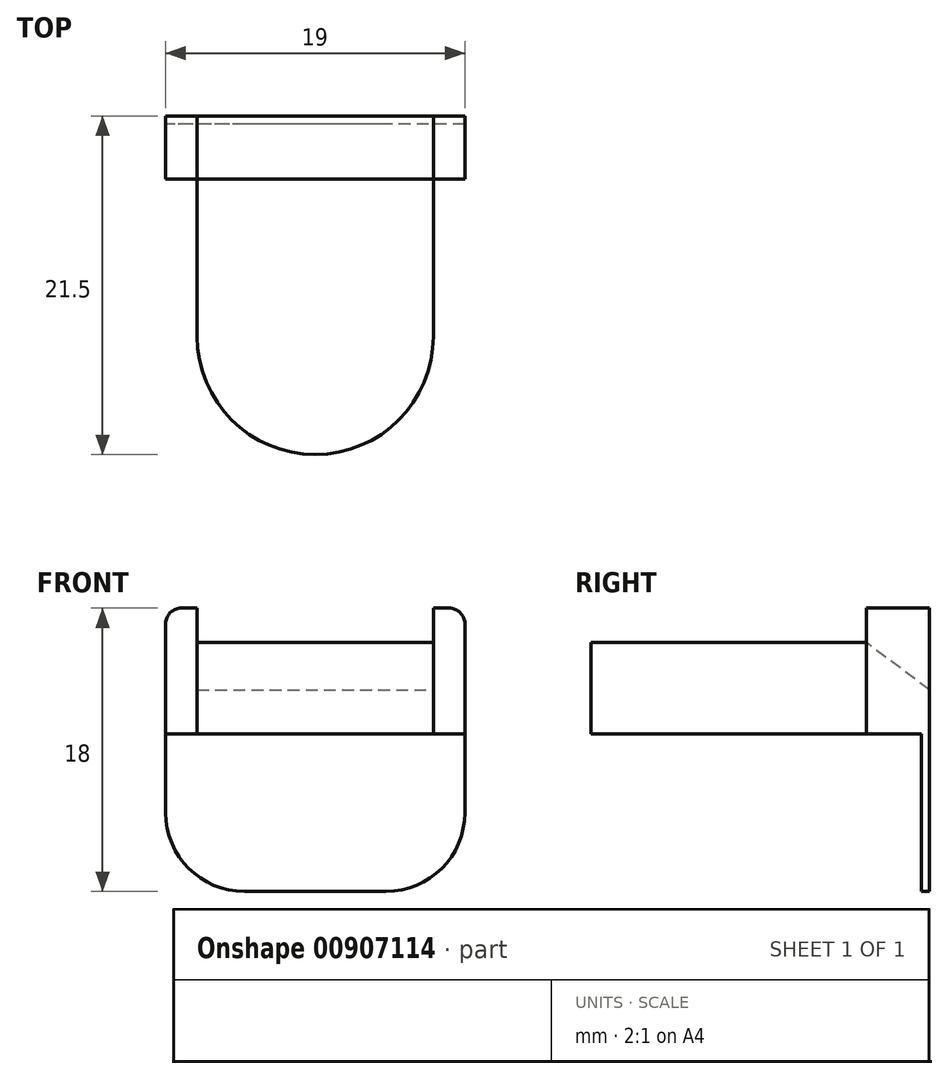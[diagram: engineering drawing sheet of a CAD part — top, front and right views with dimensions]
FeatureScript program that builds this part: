
annotation { "Feature Type Name" : "Feature", "Feature Type Description" : "" }
export const myFeature = defineFeature(function(context is Context, id is Id, definition is map)
    precondition{}
    {
        {
            var Q0;
            Q0=qCreatedBy(makeId("Top.planeOp"),FACE);
            var sketch = newSketch(context, id + "F0", { "sketchPlane" : qUnion([Q0])});
            skLineSegment(sketch, "E0", {"start": v(-7.5, 0) * mm, "end": v(-7.5, 14) * mm});
            skLineSegment(sketch, "E1", {"start": v(-7.5, 14) * mm, "end": v(7.5, 14) * mm});
            skLineSegment(sketch, "E2", {"start": v(7.5, 14) * mm, "end": v(7.5, 0) * mm});
            skArc(sketch, "E3", {"start": v(-7.5, 0) * mm, "mid": v(0, -7.5) * mm, "end": v(7.5, 0) * mm});
            skLineSegment(sketch, "E4", {"start": v(-7.5, 10) * mm, "end": v(-9.5, 10) * mm});
            skLineSegment(sketch, "E5", {"start": v(-9.5, 10) * mm, "end": v(-9.5, 14) * mm});
            skLineSegment(sketch, "E6", {"start": v(-9.5, 14) * mm, "end": v(-7.5, 14) * mm});
            skLineSegment(sketch, "E7", {"start": v(7.5, 14) * mm, "end": v(9.5, 14) * mm});
            skLineSegment(sketch, "E8", {"start": v(9.5, 14) * mm, "end": v(9.5, 10) * mm});
            skLineSegment(sketch, "E9", {"start": v(9.5, 10) * mm, "end": v(7.5, 10) * mm});
            skLineSegment(sketch, "E10", {"start": v(9.5, 13.5) * mm, "end": v(-9.5, 13.5) * mm});
            skSolve(sketch);
        }
        {
            var Q0;
            {var subQ0=sQuery(id+"F0.wireOp",EDGE,"E3");Q0=makeQuery(id+"F0.imprint","IMPRINT",FACE,{"disambiguationData":[TD([[makeQuery(id+"F0.imprint","IMPRINT",EDGE,{"derivedFrom":subQ0}),1.0]])]});}
            var Q1;
            {var subQ0=sQuery(id+"F0.wireOp",EDGE,"E1");Q1=makeQuery(id+"F0.imprint","IMPRINT",FACE,{"disambiguationData":[TD([[makeQuery(id+"F0.imprint","IMPRINT",EDGE,{"derivedFrom":subQ0}),-1.0]])]});}
            extrude(context, id + "F1", {"entities" : qUnion([Q0, Q1]), "depth" : 5.8 * mm, "offsetDistance" : 25 * mm});
        }
        {
            var Q0;
            Q0=makeQuery(id+"F1.opExtrude","CAP_EDGE",EDGE,{"disambiguationData":[OSD([sQuery(id+"F0.wireOp",EDGE,"E1")])],"isStart":false});
            chamfer(context, id + "F2", {"entities" : qUnion([Q0]), "chamferType" : ChamferType.TWO_OFFSETS, "width1" : 3 * mm, "oppositeDirection" : false, "width2" : 4 * mm, "tangentPropagation" : true});
        }
        {
            var Q0;
            {var subQ2=sQuery(id+"F0.wireOp",EDGE,"E4");Q0=makeQuery(id+"F0.imprint","IMPRINT",FACE,{"disambiguationData":[TD([[makeQuery(id+"F0.imprint","IMPRINT",EDGE,{"derivedFrom":subQ2}),-1.0]])]});}
            var Q1;
            {var subQ0=sQuery(id+"F0.wireOp",EDGE,"E7");Q1=makeQuery(id+"F0.imprint","IMPRINT",FACE,{"disambiguationData":[TD([[makeQuery(id+"F0.imprint","IMPRINT",EDGE,{"derivedFrom":subQ0}),-1.0]])]});}
            var Q2;
            {var subQ0=sQuery(id+"F0.wireOp",EDGE,"E9");Q2=makeQuery(id+"F0.imprint","IMPRINT",FACE,{"disambiguationData":[TD([[makeQuery(id+"F0.imprint","IMPRINT",EDGE,{"derivedFrom":subQ0}),-1.0]])]});}
            var Q3;
            {var subQ0=sQuery(id+"F0.wireOp",EDGE,"E6");Q3=makeQuery(id+"F0.imprint","IMPRINT",FACE,{"disambiguationData":[TD([[makeQuery(id+"F0.imprint","IMPRINT",EDGE,{"derivedFrom":subQ0}),-1.0]])]});}
            extrude(context, id + "F3", {"entities" : qUnion([Q0, Q1, Q2, Q3]), "operationType" : NewBodyOperationType.ADD, "depth" : 8 * mm, "offsetDistance" : 25 * mm});
        }
        {
            var Q0;
            {var subQ0=sQuery(id+"F0.wireOp",EDGE,"E1");Q0=makeQuery(id+"F0.imprint","IMPRINT",FACE,{"disambiguationData":[TD([[makeQuery(id+"F0.imprint","IMPRINT",EDGE,{"derivedFrom":subQ0}),-1.0]])]});}
            var Q1;
            {var subQ0=sQuery(id+"F0.wireOp",EDGE,"E7");Q1=makeQuery(id+"F0.imprint","IMPRINT",FACE,{"disambiguationData":[TD([[makeQuery(id+"F0.imprint","IMPRINT",EDGE,{"derivedFrom":subQ0}),-1.0]])]});}
            var Q2;
            {var subQ0=sQuery(id+"F0.wireOp",EDGE,"E6");Q2=makeQuery(id+"F0.imprint","IMPRINT",FACE,{"disambiguationData":[TD([[makeQuery(id+"F0.imprint","IMPRINT",EDGE,{"derivedFrom":subQ0}),-1.0]])]});}
            extrude(context, id + "F4", {"entities" : qUnion([Q0, Q1, Q2]), "operationType" : NewBodyOperationType.ADD, "oppositeDirection" : true, "depth" : 10 * mm, "offsetDistance" : 25 * mm});
        }
        {
            var Q0;
            Q0=makeQuery(id+"F3.opExtrude","CAP_EDGE",EDGE,{"disambiguationData":[OSD([sQuery(id+"F0.wireOp",EDGE,"E5")])],"isStart":false});
            var Q1;
            Q1=makeQuery(id+"F3.opExtrude","CAP_EDGE",EDGE,{"disambiguationData":[OSD([sQuery(id+"F0.wireOp",EDGE,"E8")])],"isStart":false});
            fillet(context, id + "F5", {"entities" : qUnion([Q0, Q1]), "radius" : 1 * mm, "tangentPropagation" : true, "allowEdgeOverflow" : false});
        }
        {
            var Q0;
            Q0=makeQuery(id+"F4.opExtrude","CAP_EDGE",EDGE,{"disambiguationData":[OSD([sQuery(id+"F0.wireOp",EDGE,"E8")])],"isStart":false});
            var Q1;
            Q1=makeQuery(id+"F4.opExtrude","CAP_EDGE",EDGE,{"disambiguationData":[OSD([sQuery(id+"F0.wireOp",EDGE,"E5")])],"isStart":false});
            fillet(context, id + "F6", {"entities" : qUnion([Q0, Q1]), "radius" : 5 * mm, "tangentPropagation" : true, "allowEdgeOverflow" : false});
        }
    });
